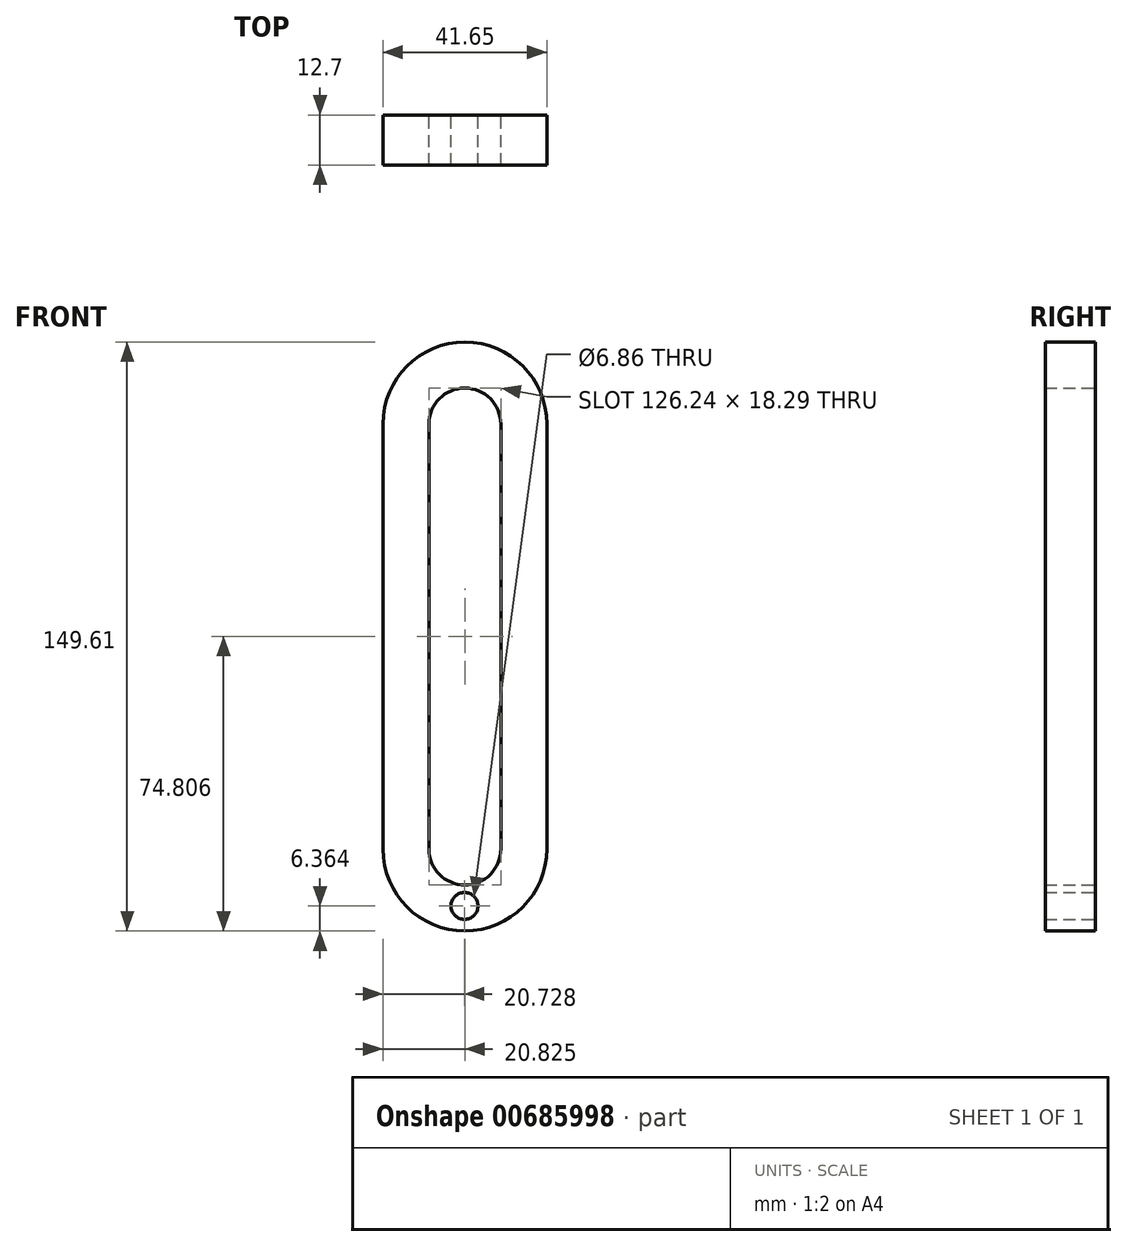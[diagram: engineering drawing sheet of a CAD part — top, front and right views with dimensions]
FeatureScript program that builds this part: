
annotation { "Feature Type Name" : "Feature", "Feature Type Description" : "" }
export const myFeature = defineFeature(function(context is Context, id is Id, definition is map)
    precondition{}
    {
        {
            var Q0;
            Q0=qCreatedBy(makeId("Front.planeOp"),FACE);
            var sketch = newSketch(context, id + "F0", { "sketchPlane" : qUnion([Q0])});
            skLineSegment(sketch, "E0", {"start": v(-9.29, 52.7) * mm, "end": v(-9.29, -55.25) * mm});
            skLineSegment(sketch, "E1", {"start": v(9, 52.7) * mm, "end": v(9, -55.25) * mm});
            skArc(sketch, "E2", {"start": v(9, 52.7) * mm, "mid": v(-0.15, 61.84) * mm, "end": v(-9.29, 52.7) * mm});
            skArc(sketch, "E3", {"start": v(-9.29, -55.25) * mm, "mid": v(-0.15, -64.4) * mm, "end": v(9, -55.25) * mm});
            skPoint(sketch, "E4.centerSnap0", {"position": v(-0.15, -64.4) * mm});
            skLineSegment(sketch, "E5", {"start": v(-20.97, 52.7) * mm, "end": v(-20.97, -55.25) * mm});
            skLineSegment(sketch, "E6", {"start": v(20.68, 52.7) * mm, "end": v(20.68, -55.25) * mm});
            skArc(sketch, "E7", {"start": v(20.68, 52.7) * mm, "mid": v(-0.15, 73.53) * mm, "end": v(-20.97, 52.7) * mm});
            skArc(sketch, "E8", {"start": v(-20.97, -55.25) * mm, "mid": v(-0.15, -76.08) * mm, "end": v(20.68, -55.25) * mm});
            skCircle(sketch, "E9", {"center": v(-0.24, -69.72) * mm, "radius": 3.43 * mm});
            skSolve(sketch);
        }
        {
            var Q0;
            Q0 = qSketchRegion(id + "F0", true);
            extrude(context, id + "F1", {"entities" : qUnion([Q0]), "depth" : 12.7 * mm, "offsetDistance" : 25.4 * mm});
        }
    });
